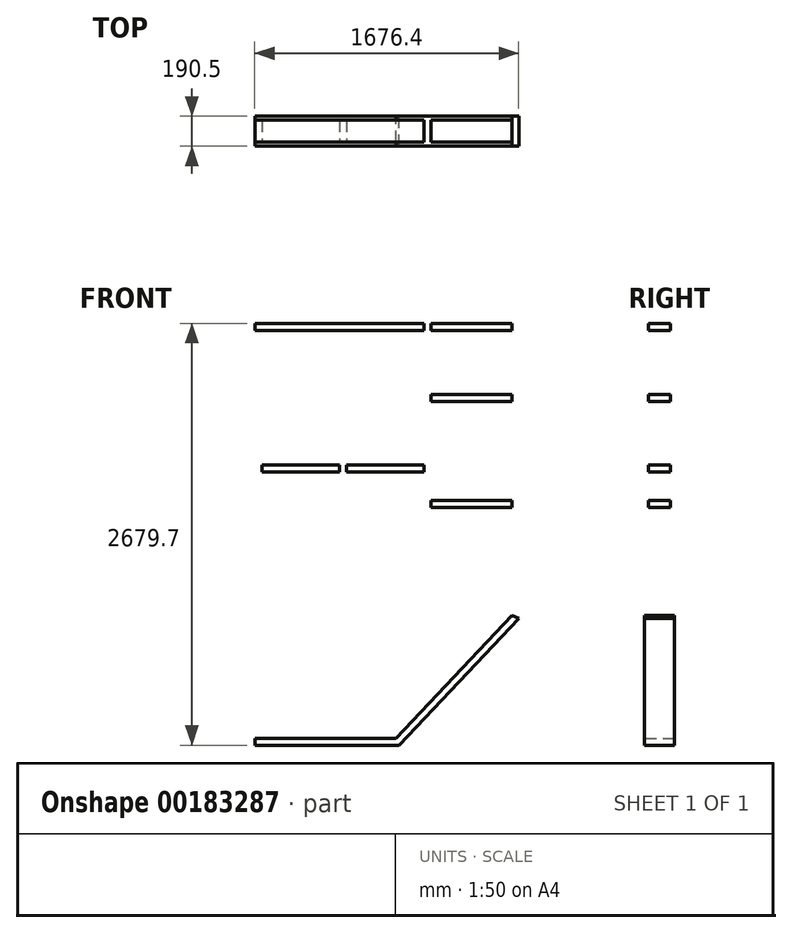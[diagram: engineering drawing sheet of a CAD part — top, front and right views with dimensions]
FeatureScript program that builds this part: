
annotation { "Feature Type Name" : "Feature", "Feature Type Description" : "" }
export const myFeature = defineFeature(function(context is Context, id is Id, definition is map)
    precondition{}
    {
        {
            var Q0;
            Q0=qCreatedBy(makeId("Front.planeOp"),FACE);
            var sketch = newSketch(context, id + "F0", { "sketchPlane" : qUnion([Q0])});
            skLineSegment(sketch, "E0", {"start": v(-1544.64, -1957.68) * mm, "end": v(-1544.64, 2144.42) * mm});
            skLineSegment(sketch, "E1", {"start": v(-1544.64, -1957.68) * mm, "end": v(-1455.74, -1957.68) * mm});
            skLineSegment(sketch, "E2", {"start": v(-1455.74, -1957.68) * mm, "end": v(-1455.74, -2110.08) * mm});
            skLineSegment(sketch, "E3", {"start": v(-1455.74, -2110.08) * mm, "end": v(-1697.04, -2110.08) * mm});
            skLineSegment(sketch, "E4", {"start": v(-1697.04, -2110.08) * mm, "end": v(-1697.04, 2296.82) * mm});
            skLineSegment(sketch, "E5", {"start": v(-1544.64, 2144.42) * mm, "end": v(-471.49, 2144.42) * mm});
            skLineSegment(sketch, "E6", {"start": v(-1697.04, 2296.82) * mm, "end": v(-623.89, 2296.82) * mm});
            skLineSegment(sketch, "E7", {"start": v(-471.49, 2144.42) * mm, "end": v(-471.49, 2607.97) * mm});
            skLineSegment(sketch, "E8", {"start": v(-623.89, 2296.82) * mm, "end": v(-623.89, 2760.37) * mm});
            skLineSegment(sketch, "E9", {"start": v(-471.49, 2607.97) * mm, "end": v(131.76, 2607.97) * mm});
            skLineSegment(sketch, "E10", {"start": v(-623.89, 2760.37) * mm, "end": v(-20.64, 2760.37) * mm});
            skLineSegment(sketch, "E11", {"start": v(-20.64, 2760.37) * mm, "end": v(-20.64, 2785.77) * mm});
            skLineSegment(sketch, "E12", {"start": v(-20.64, 2785.77) * mm, "end": v(1427.16, 2785.77) * mm});
            skLineSegment(sketch, "E13", {"start": v(131.76, 2607.97) * mm, "end": v(131.76, 2760.37) * mm});
            skLineSegment(sketch, "E14", {"start": v(131.76, 2760.37) * mm, "end": v(1223.96, 2760.37) * mm});
            skLineSegment(sketch, "E15", {"start": v(1427.16, 2785.77) * mm, "end": v(1427.16, 2760.37) * mm});
            skLineSegment(sketch, "E16", {"start": v(1223.96, 2760.37) * mm, "end": v(1223.96, 2607.97) * mm});
            skLineSegment(sketch, "E17", {"start": v(1223.96, 2607.97) * mm, "end": v(1325.56, 2607.97) * mm});
            skLineSegment(sketch, "E18", {"start": v(1427.16, 2760.37) * mm, "end": v(1477.96, 2760.37) * mm});
            skLineSegment(sketch, "E19", {"start": v(1325.56, 2607.97) * mm, "end": v(1325.56, -1233.78) * mm});
            skLineSegment(sketch, "E20", {"start": v(1325.56, -1233.78) * mm, "end": v(588.96, -1233.78) * mm});
            skLineSegment(sketch, "E21", {"start": v(588.96, -1233.78) * mm, "end": v(588.96, -1386.18) * mm});
            skLineSegment(sketch, "E22", {"start": v(588.96, -1386.18) * mm, "end": v(931.86, -1386.18) * mm});
            skLineSegment(sketch, "E23", {"start": v(-1455.74, -1957.68) * mm, "end": v(-573.09, -1957.68) * mm});
            skLineSegment(sketch, "E24", {"start": v(-1455.74, -2110.08) * mm, "end": v(-573.09, -2110.08) * mm});
            skLineSegment(sketch, "E25", {"start": v(-573.09, -2110.08) * mm, "end": v(-573.09, -1957.68) * mm});
            skLineSegment(sketch, "E26", {"start": v(-573.09, -1957.68) * mm, "end": v(-509.59, -1957.68) * mm});
            skLineSegment(sketch, "E27", {"start": v(931.86, -1386.18) * mm, "end": v(931.86, -1957.68) * mm});
            skLineSegment(sketch, "E28", {"start": v(931.86, -1957.68) * mm, "end": v(-357.19, -1957.68) * mm});
            skLineSegment(sketch, "E29", {"start": v(-509.59, -1957.68) * mm, "end": v(-509.59, -1233.78) * mm});
            skLineSegment(sketch, "E30", {"start": v(-509.59, -1233.78) * mm, "end": v(-204.79, -1233.78) * mm});
            skLineSegment(sketch, "E31", {"start": v(-357.19, -1957.68) * mm, "end": v(-357.19, -1386.18) * mm});
            skLineSegment(sketch, "E32", {"start": v(588.96, -1233.78) * mm, "end": v(-166.69, -1233.78) * mm});
            skLineSegment(sketch, "E33", {"start": v(588.96, -1386.18) * mm, "end": v(-166.69, -1386.18) * mm});
            skLineSegment(sketch, "E34", {"start": v(-166.69, -1233.78) * mm, "end": v(-166.69, -1386.18) * mm});
            skLineSegment(sketch, "E35", {"start": v(-357.19, -1386.18) * mm, "end": v(-204.79, -1386.18) * mm});
            skLineSegment(sketch, "E36", {"start": v(-204.79, -1233.78) * mm, "end": v(-204.79, -1386.18) * mm});
            skLineSegment(sketch, "E37", {"start": v(-573.09, -2110.08) * mm, "end": v(1084.26, -2110.08) * mm});
            skLineSegment(sketch, "E38", {"start": v(1084.26, -2110.08) * mm, "end": v(1084.26, -1386.18) * mm});
            skLineSegment(sketch, "E39", {"start": v(1084.26, -1386.18) * mm, "end": v(1477.96, -1386.18) * mm});
            skLineSegment(sketch, "E40", {"start": v(1477.96, -1386.18) * mm, "end": v(1477.96, 2760.37) * mm});
            skLineSegment(sketch, "E41", {"start": v(-204.79, -1386.18) * mm, "end": v(-166.69, -1386.18) * mm});
            skLineSegment(sketch, "E42", {"start": v(-204.79, -1233.78) * mm, "end": v(-166.69, -1233.78) * mm});
            skLineSegment(sketch, "E43", {"start": v(131.76, 2607.97) * mm, "end": v(1223.96, 2607.97) * mm});
            skLineSegment(sketch, "E44.top", {"start": v(-1544.64, 2099.97) * mm, "end": v(-471.49, 2099.97) * mm});
            skLineSegment(sketch, "E44.left", {"start": v(-1544.64, 2144.42) * mm, "end": v(-1544.64, 2099.97) * mm});
            skLineSegment(sketch, "E44.right", {"start": v(87.31, 2144.42) * mm, "end": v(87.31, 2099.97) * mm});
            skLineSegment(sketch, "E45.bottom", {"start": v(-1544.64, 2099.97) * mm, "end": v(-1500.19, 2099.97) * mm});
            skLineSegment(sketch, "E45.top", {"start": v(-1544.64, -490.83) * mm, "end": v(-1500.19, -490.83) * mm});
            skLineSegment(sketch, "E45.left", {"start": v(-1544.64, 2099.97) * mm, "end": v(-1544.64, -490.83) * mm});
            skLineSegment(sketch, "E45.right", {"start": v(-1500.19, 2099.97) * mm, "end": v(-1500.19, -490.83) * mm});
            skLineSegment(sketch, "E46.bottom", {"start": v(-471.49, 2607.97) * mm, "end": v(-427.04, 2607.97) * mm});
            skLineSegment(sketch, "E46.left", {"start": v(-471.49, 2607.97) * mm, "end": v(-471.49, 2144.42) * mm});
            skLineSegment(sketch, "E46.right", {"start": v(-427.04, 2607.97) * mm, "end": v(-427.04, 2144.42) * mm});
            skLineSegment(sketch, "E47.bottom", {"start": v(131.76, 2607.97) * mm, "end": v(87.31, 2607.97) * mm});
            skLineSegment(sketch, "E47.left", {"start": v(131.76, 2607.97) * mm, "end": v(131.76, 271.17) * mm});
            skLineSegment(sketch, "E47.right", {"start": v(87.31, 2607.97) * mm, "end": v(87.31, 289.59) * mm});
            skLineSegment(sketch, "E48.bottom", {"start": v(-1544.64, -490.83) * mm, "end": v(-648.65, -490.83) * mm});
            skLineSegment(sketch, "E48.top", {"start": v(-1544.64, -535.28) * mm, "end": v(-630.24, -535.28) * mm});
            skLineSegment(sketch, "E48.left", {"start": v(-1544.64, -490.83) * mm, "end": v(-1544.64, -535.28) * mm});
            skLineSegment(sketch, "E49", {"start": v(-630.24, -535.28) * mm, "end": v(-648.65, -490.83) * mm});
            skLineSegment(sketch, "E50", {"start": v(131.76, 271.17) * mm, "end": v(87.31, 289.59) * mm});
            skLineSegment(sketch, "E51", {"start": v(-630.24, -535.28) * mm, "end": v(131.76, 271.17) * mm});
            skLineSegment(sketch, "E52", {"start": v(-648.65, -490.83) * mm, "end": v(87.31, 289.59) * mm});
            skLineSegment(sketch, "E53.bottom", {"start": v(-427.04, 2607.97) * mm, "end": v(87.31, 2607.97) * mm});
            skLineSegment(sketch, "E53.top", {"start": v(-427.04, 2563.52) * mm, "end": v(87.31, 2563.52) * mm});
            skLineSegment(sketch, "E53.left", {"start": v(-427.04, 2607.97) * mm, "end": v(-427.04, 2563.52) * mm});
            skLineSegment(sketch, "E53.right", {"start": v(87.31, 2607.97) * mm, "end": v(87.31, 2563.52) * mm});
            skLineSegment(sketch, "E54.bottom", {"start": v(87.31, 289.59) * mm, "end": v(-1500.19, 289.59) * mm});
            skLineSegment(sketch, "E54.top", {"start": v(87.31, 334.04) * mm, "end": v(-1500.19, 334.04) * mm});
            skLineSegment(sketch, "E54.left", {"start": v(87.31, 289.59) * mm, "end": v(87.31, 334.04) * mm});
            skLineSegment(sketch, "E54.right", {"start": v(-1500.19, 289.59) * mm, "end": v(-1500.19, 334.04) * mm});
            skLineSegment(sketch, "E55.bottom", {"start": v(-648.65, -490.83) * mm, "end": v(-693.1, -490.83) * mm});
            skLineSegment(sketch, "E55.top", {"start": v(-648.65, 289.59) * mm, "end": v(-693.1, 289.59) * mm});
            skLineSegment(sketch, "E55.left", {"start": v(-648.65, -490.83) * mm, "end": v(-648.65, 289.59) * mm});
            skLineSegment(sketch, "E55.right", {"start": v(-693.1, -490.83) * mm, "end": v(-693.1, 289.59) * mm});
            skLineSegment(sketch, "E56.top", {"start": v(-471.49, 334.04) * mm, "end": v(-427.04, 334.04) * mm});
            skLineSegment(sketch, "E56.left", {"start": v(-471.49, 2144.42) * mm, "end": v(-471.49, 334.04) * mm});
            skLineSegment(sketch, "E56.right", {"start": v(-427.04, 2144.42) * mm, "end": v(-427.04, 334.04) * mm});
            skLineSegment(sketch, "E57.trimOffspring", {"start": v(-427.04, 2099.97) * mm, "end": v(87.31, 2099.97) * mm});
            skLineSegment(sketch, "E58.trimOffspring", {"start": v(-427.04, 2144.42) * mm, "end": v(87.31, 2144.42) * mm});
            skLineSegment(sketch, "E59.bottom", {"start": v(-1008.06, 2099.97) * mm, "end": v(-963.61, 2099.97) * mm});
            skLineSegment(sketch, "E59.top", {"start": v(-1008.06, 334.04) * mm, "end": v(-963.61, 334.04) * mm});
            skLineSegment(sketch, "E59.left", {"start": v(-1008.06, 2099.97) * mm, "end": v(-1008.06, 334.04) * mm});
            skLineSegment(sketch, "E59.right", {"start": v(-963.61, 2099.97) * mm, "end": v(-963.61, 334.04) * mm});
            skLineSegment(sketch, "E60.bottom", {"start": v(-1119.19, 289.59) * mm, "end": v(-1074.74, 289.59) * mm});
            skLineSegment(sketch, "E60.top", {"start": v(-1119.19, -490.83) * mm, "end": v(-1074.74, -490.83) * mm});
            skLineSegment(sketch, "E60.left", {"start": v(-1119.19, 289.59) * mm, "end": v(-1119.19, -490.83) * mm});
            skLineSegment(sketch, "E60.right", {"start": v(-1074.74, 289.59) * mm, "end": v(-1074.74, -490.83) * mm});
            skLineSegment(sketch, "E61.bottom", {"start": v(87.31, 1693.57) * mm, "end": v(-427.04, 1693.57) * mm});
            skLineSegment(sketch, "E61.top", {"start": v(87.31, 1649.12) * mm, "end": v(-427.04, 1649.12) * mm});
            skLineSegment(sketch, "E61.left", {"start": v(87.31, 1693.57) * mm, "end": v(87.31, 1649.12) * mm});
            skLineSegment(sketch, "E61.right", {"start": v(-427.04, 1693.57) * mm, "end": v(-427.04, 1649.12) * mm});
            skLineSegment(sketch, "E62.bottom", {"start": v(-427.04, 1020.1) * mm, "end": v(87.31, 1020.1) * mm});
            skLineSegment(sketch, "E62.top", {"start": v(-427.04, 975.64) * mm, "end": v(87.31, 975.64) * mm});
            skLineSegment(sketch, "E62.left", {"start": v(-427.04, 1020.1) * mm, "end": v(-427.04, 975.64) * mm});
            skLineSegment(sketch, "E62.right", {"start": v(87.31, 1020.1) * mm, "end": v(87.31, 975.64) * mm});
            skLineSegment(sketch, "E63.bottom", {"start": v(-963.61, 1245.52) * mm, "end": v(-471.49, 1245.52) * mm});
            skLineSegment(sketch, "E63.top", {"start": v(-963.61, 1201.07) * mm, "end": v(-471.49, 1201.07) * mm});
            skLineSegment(sketch, "E63.left", {"start": v(-963.61, 1245.52) * mm, "end": v(-963.61, 1201.07) * mm});
            skLineSegment(sketch, "E63.right", {"start": v(-471.49, 1245.52) * mm, "end": v(-471.49, 1201.07) * mm});
            skLineSegment(sketch, "E64.bottom", {"start": v(-1008.06, 1245.52) * mm, "end": v(-1500.19, 1245.52) * mm});
            skLineSegment(sketch, "E64.top", {"start": v(-1008.06, 1201.07) * mm, "end": v(-1500.19, 1201.07) * mm});
            skLineSegment(sketch, "E64.left", {"start": v(-1008.06, 1245.52) * mm, "end": v(-1008.06, 1201.07) * mm});
            skLineSegment(sketch, "E64.right", {"start": v(-1500.19, 1245.52) * mm, "end": v(-1500.19, 1201.07) * mm});
            skSolve(sketch);
        }
        {
            var Q0;
            Q0=makeQuery(id+"F0.imprint","IMPRINT",FACE,{"disambiguationData":[TD([[makeQuery(id+"F0.imprint","IMPRINT",EDGE,{"derivedFrom":sQuery(id+"F0.wireOp",EDGE,"E49")}),-1.0]])]});
            var Q1;
            Q1=makeQuery(id+"F0.imprint","IMPRINT",FACE,{"disambiguationData":[TD([[makeQuery(id+"F0.imprint","IMPRINT",EDGE,{"derivedFrom":sQuery(id+"F0.wireOp",EDGE,"E47.bottom")}),1.0]])]});
            var Q2;
            Q2=makeQuery(id+"F0.imprint","IMPRINT",FACE,{"disambiguationData":[TD([[makeQuery(id+"F0.imprint","IMPRINT",EDGE,{"derivedFrom":sQuery(id+"F0.wireOp",EDGE,"E48.top")}),1.0]])]});
            extrude(context, id + "F1", {"entities" : qUnion([Q0, Q1, Q2]), "depth" : 25.4 * mm});
        }
        {
            var Q0;
            Q0=makeQuery(id+"F1.opExtrude","CAP_FACE",FACE,{"disambiguationData":[OSD([sQuery(id+"F0.wireOp",EDGE,"E47.bottom"),sQuery(id+"F0.wireOp",EDGE,"E47.left"),sQuery(id+"F0.wireOp",EDGE,"E47.right"),sQuery(id+"F0.wireOp",EDGE,"E48.bottom"),sQuery(id+"F0.wireOp",EDGE,"E48.top"),sQuery(id+"F0.wireOp",EDGE,"E48.left"),sQuery(id+"F0.wireOp",EDGE,"E51"),sQuery(id+"F0.wireOp",EDGE,"E52"),sQuery(id+"F0.wireOp",EDGE,"E53.right"),sQuery(id+"F0.wireOp",EDGE,"E54.left"),sQuery(id+"F0.wireOp",EDGE,"E55.bottom"),sQuery(id+"F0.wireOp",EDGE,"E60.top"),sQuery(id+"F0.wireOp",EDGE,"E61.left"),sQuery(id+"F0.wireOp",EDGE,"E62.right")])],"isStart":true});
            extrude(context, id + "F2", {"entities" : qUnion([Q0]), "operationType" : NewBodyOperationType.ADD, "depth" : 165.1 * mm});
        }
        {
            var Q0;
            Q0=makeQuery(id+"F0.imprint","IMPRINT",FACE,{"disambiguationData":[TD([[makeQuery(id+"F0.imprint","IMPRINT",EDGE,{"derivedFrom":sQuery(id+"F0.wireOp",EDGE,"E46.bottom")}),-1.0]])]});
            var Q1;
            Q1=makeQuery(id+"F0.imprint","IMPRINT",FACE,{"disambiguationData":[TD([[makeQuery(id+"F0.imprint","IMPRINT",EDGE,{"derivedFrom":sQuery(id+"F0.wireOp",EDGE,"E62.bottom")}),-1.0]])]});
            var Q2;
            Q2=makeQuery(id+"F0.imprint","IMPRINT",FACE,{"disambiguationData":[TD([[makeQuery(id+"F0.imprint","IMPRINT",EDGE,{"derivedFrom":sQuery(id+"F0.wireOp",EDGE,"E61.bottom")}),1.0]])]});
            var Q3;
            {var subQ1=sQuery(id+"F0.wireOp",EDGE,"E54.left");Q3=makeQuery(id+"F0.imprint","IMPRINT",FACE,{"disambiguationData":[TD([[makeQuery(id+"F0.imprint","IMPRINT",EDGE,{"derivedFrom":subQ1}),1.0]])]});}
            var Q4;
            Q4=makeQuery(id+"F0.imprint","IMPRINT",FACE,{"disambiguationData":[TD([[makeQuery(id+"F0.imprint","IMPRINT",EDGE,{"derivedFrom":sQuery(id+"F0.wireOp",EDGE,"E55.bottom")}),-1.0]])]});
            var Q5;
            {var subQ3=sQuery(id+"F0.wireOp",EDGE,"E45.bottom");Q5=makeQuery(id+"F0.imprint","IMPRINT",FACE,{"disambiguationData":[TD([[makeQuery(id+"F0.imprint","IMPRINT",EDGE,{"derivedFrom":subQ3}),-1.0]])]});}
            var Q6;
            Q6=makeQuery(id+"F0.imprint","IMPRINT",FACE,{"disambiguationData":[TD([[makeQuery(id+"F0.imprint","IMPRINT",EDGE,{"derivedFrom":sQuery(id+"F0.wireOp",EDGE,"E60.bottom")}),-1.0]])]});
            var Q7;
            {var subQ4=sQuery(id+"F0.wireOp",EDGE,"E59.bottom");Q7=makeQuery(id+"F0.imprint","IMPRINT",FACE,{"disambiguationData":[TD([[makeQuery(id+"F0.imprint","IMPRINT",EDGE,{"derivedFrom":subQ4}),-1.0]])]});}
            var Q8;
            Q8=makeQuery(id+"F0.imprint","IMPRINT",FACE,{"disambiguationData":[TD([[makeQuery(id+"F0.imprint","IMPRINT",EDGE,{"derivedFrom":sQuery(id+"F0.wireOp",EDGE,"E64.bottom")}),1.0]])]});
            var Q9;
            Q9=makeQuery(id+"F0.imprint","IMPRINT",FACE,{"disambiguationData":[TD([[makeQuery(id+"F0.imprint","IMPRINT",EDGE,{"derivedFrom":sQuery(id+"F0.wireOp",EDGE,"E63.bottom")}),-1.0]])]});
            var Q10;
            {var subQ0=sQuery(id+"F0.wireOp",EDGE,"E57.trimOffspring");Q10=makeQuery(id+"F0.imprint","IMPRINT",FACE,{"disambiguationData":[TD([[makeQuery(id+"F0.imprint","IMPRINT",EDGE,{"derivedFrom":subQ0}),1.0]])]});}
            var Q11;
            {var subQ5=sQuery(id+"F0.wireOp",EDGE,"E5");Q11=makeQuery(id+"F0.imprint","IMPRINT",FACE,{"disambiguationData":[TD([[makeQuery(id+"F0.imprint","IMPRINT",EDGE,{"derivedFrom":subQ5}),-1.0]])]});}
            var Q12;
            Q12=makeQuery(id+"F0.imprint","IMPRINT",FACE,{"disambiguationData":[TD([[makeQuery(id+"F0.imprint","IMPRINT",EDGE,{"derivedFrom":sQuery(id+"F0.wireOp",EDGE,"E53.bottom")}),-1.0]])]});
            extrude(context, id + "F3", {"entities" : qUnion([Q0, Q1, Q2, Q3, Q4, Q5, Q6, Q7, Q8, Q9, Q10, Q11, Q12]), "operationType" : NewBodyOperationType.ADD, "oppositeDirection" : true, "depth" : 139.7 * mm});
        }
    });
